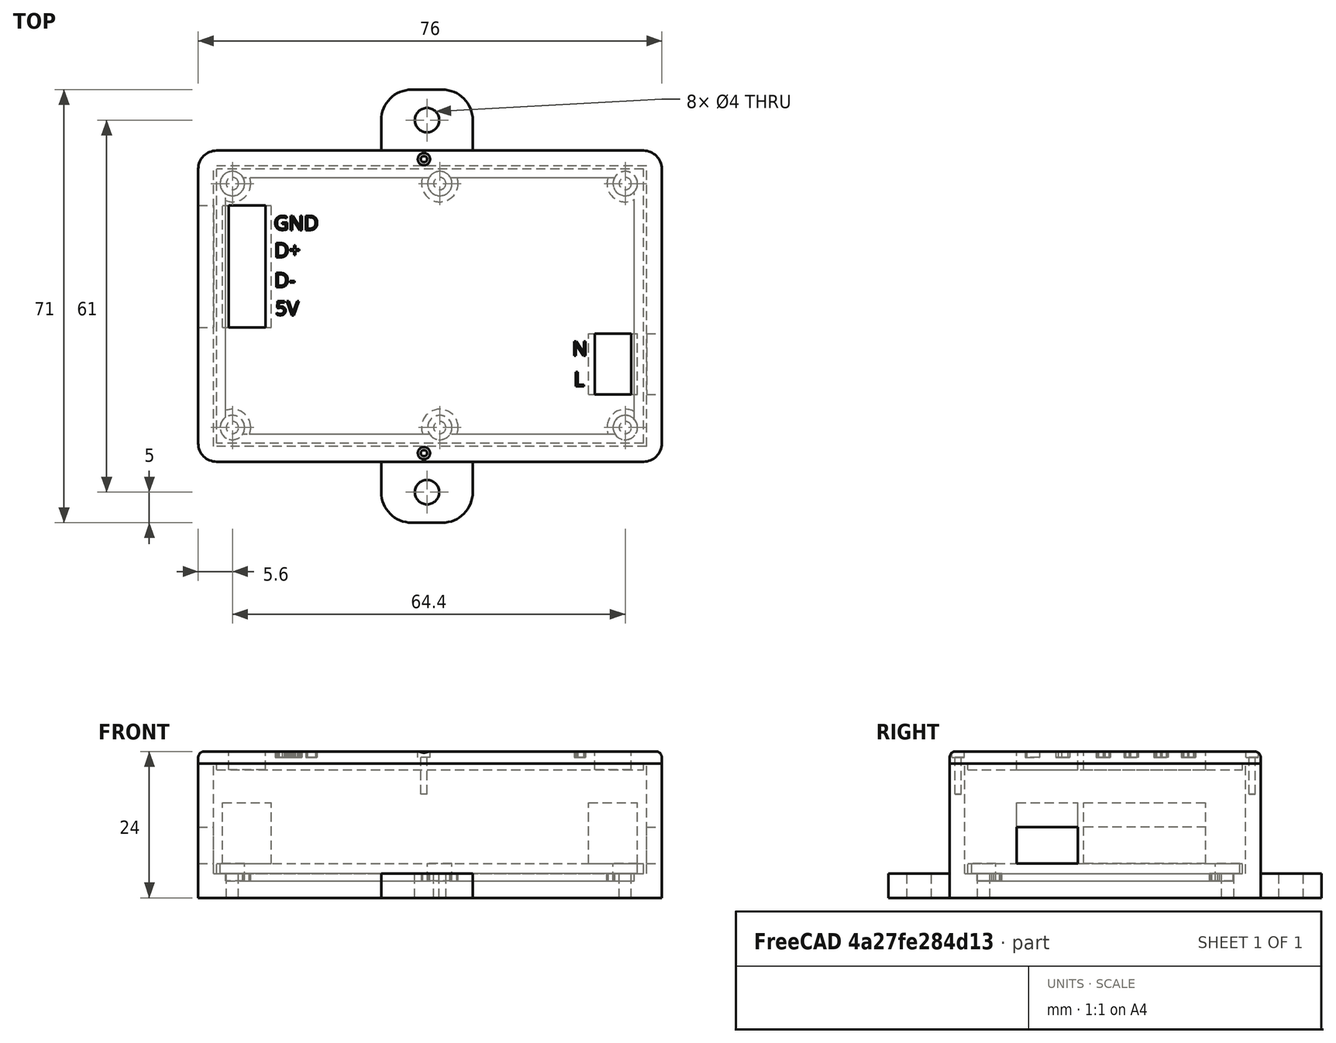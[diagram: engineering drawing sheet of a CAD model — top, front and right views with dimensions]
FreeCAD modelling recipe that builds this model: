
FCSTD DOCUMENT  (FreeCAD 0.17R13522 (Git))
Label: Caja Bridge TCP-RTU V1-230V
License: All rights reserved
LicenseURL: http://en.wikipedia.org/wiki/All_rights_reserved
objects: Part::Cylinder×26, Part::Cut×18, Part::Box×15, Part::MultiFuse×15, Part::Part2DObjectPython×6, Part::Extrusion×6, Part::Fillet×4
note: 90 computed .brp shape members not serialized (recipe doc carries the construction recipe); baked Part::Feature solids carry a one-line shape summary decoded from their .brp

FEATURE [Part::Box] Box  label="Cubo"
  AttacherType = Attacher::AttachEngine3D
  Height = 1.6
  Length = 70
  Width = 45
FEATURE [Part::Cylinder] Cylinder  label="Cilindro"
  Angle = 360
  AttacherType = Attacher::AttachEngine3D
  Height = 10
  Placement = pos=(2.6,2.6,-5) rot=(0,0,1;0rad)
  Radius = 2
FEATURE [Part::Cylinder] Cylinder001  label="Cilindro001"
  Angle = 360
  AttacherType = Attacher::AttachEngine3D
  Height = 10
  Placement = pos=(36.6,2.6,-5) rot=(0,0,1;0rad)
  Radius = 2
FEATURE [Part::Cylinder] Cylinder002  label="Cilindro002"
  Angle = 360
  AttacherType = Attacher::AttachEngine3D
  Height = 10
  Placement = pos=(36.6,42.6,-5) rot=(0,0,1;0rad)
  Radius = 2
FEATURE [Part::Cylinder] Cylinder003  label="Cilindro003"
  Angle = 360
  AttacherType = Attacher::AttachEngine3D
  Height = 10
  Placement = pos=(2.6,42.6,-5) rot=(0,0,1;0rad)
  Radius = 2
FEATURE [Part::Box] Box001  label="Cubo001"
  AttacherType = Attacher::AttachEngine3D
  Height = 10
  Length = 8
  Placement = pos=(1,19,1.6) rot=(0,0,1;0rad)
  Width = 20
FEATURE [Part::Box] Box002  label="Cubo002"
  AttacherType = Attacher::AttachEngine3D
  Height = 20
  Length = 71
  Placement = pos=(-0.5,-0.5,0) rot=(0,0,1;0rad)
  Width = 46
FEATURE [Part::Box] Box003  label="Cubo003"
  AttacherType = Attacher::AttachEngine3D
  Height = 22
  Length = 76
  Placement = pos=(-3,-3,-4) rot=(0,0,1;0rad)
  Width = 51
FEATURE [Part::Box] Box004  label="Cubo004"
  AttacherType = Attacher::AttachEngine3D
  Height = 1.5
  Length = 67
  Placement = pos=(1.5,1.5,-1.2) rot=(0,0,1;0rad)
  Width = 42
FEATURE [Part::MultiFuse] Fusion
  Refine = true
  Shapes = -> [Box,Box004]
FEATURE [Part::MultiFuse] Fusion001
  Refine = true
  Shapes = -> [Fusion,Box001]
FEATURE [Part::MultiFuse] Fusion002
  Refine = true
  Shapes = -> [Cylinder,Cylinder003,Cylinder002,Cylinder001]
FEATURE [Part::Cut] Cut  label="Electronica"
  Base = -> Fusion001
  Refine = true
  Tool = -> Fusion002
FEATURE [Part::Box] Box005  label="Cubo005"
  AttacherType = Attacher::AttachEngine3D
  Height = 1.5
  Length = 67
  Placement = pos=(1.5,1.5,-1.2) rot=(0,0,1;0rad)
  Width = 42
FEATURE [Part::MultiFuse] Fusion003
  Refine = true
  Shapes = -> [Box002,Box005]
FEATURE [Part::Box] Box006  label="Cubo006"
  AttacherType = Attacher::AttachEngine3D
  Height = 6
  Length = 22
  Placement = pos=(-10,19,1.6) rot=(0,0,1;0rad)
  Width = 20
FEATURE [Part::Box] Box007  label="Cubo007"
  AttacherType = Attacher::AttachEngine3D
  Height = 2
  Length = 76
  Placement = pos=(-3,-3,18) rot=(0,0,1;0rad)
  Width = 51
FEATURE [Part::Box] Box008  label="Cubo008"
  AttacherType = Attacher::AttachEngine3D
  Height = 3
  Length = 70
  Placement = pos=(0,0,17) rot=(0,0,1;0rad)
  Width = 45
FEATURE [Part::Cylinder] Cylinder004  label="Cilindro004"
  Angle = 360
  AttacherType = Attacher::AttachEngine3D
  Height = 10
  Placement = pos=(2.6,2.6,-5) rot=(0,0,1;0rad)
  Radius = 1
FEATURE [Part::Cylinder] Cylinder005  label="Cilindro005"
  Angle = 360
  AttacherType = Attacher::AttachEngine3D
  Height = 10
  Placement = pos=(36.6,2.6,-5) rot=(0,0,1;0rad)
  Radius = 1
FEATURE [Part::Cylinder] Cylinder006  label="Cilindro006"
  Angle = 360
  AttacherType = Attacher::AttachEngine3D
  Height = 10
  Placement = pos=(36.6,42.6,-5) rot=(0,0,1;0rad)
  Radius = 1
FEATURE [Part::Cylinder] Cylinder007  label="Cilindro007"
  Angle = 360
  AttacherType = Attacher::AttachEngine3D
  Height = 10
  Placement = pos=(2.6,42.6,-5) rot=(0,0,1;0rad)
  Radius = 1
FEATURE [Part::Cylinder] Cylinder008  label="Cilindro008"
  Angle = 360
  AttacherType = Attacher::AttachEngine3D
  Height = 3
  Placement = pos=(2.6,42.6,-3) rot=(0,0,1;0rad)
  Radius = 3
FEATURE [Part::Cylinder] Cylinder009  label="Cilindro009"
  Angle = 360
  AttacherType = Attacher::AttachEngine3D
  Height = 3
  Placement = pos=(36.6,2.6,-3) rot=(0,0,1;0rad)
  Radius = 3
FEATURE [Part::Cylinder] Cylinder010  label="Cilindro010"
  Angle = 360
  AttacherType = Attacher::AttachEngine3D
  Height = 3
  Placement = pos=(2.6,2.6,-3) rot=(0,0,1;0rad)
  Radius = 3
FEATURE [Part::Cylinder] Cylinder011  label="Cilindro011"
  Angle = 360
  AttacherType = Attacher::AttachEngine3D
  Height = 3
  Placement = pos=(36.6,42.6,-3) rot=(0,0,1;0rad)
  Radius = 3
FEATURE [Part::Cut] Cut001
  Base = -> Box003
  Refine = true
  Tool = -> Fusion003
FEATURE [Part::Cut] Cut002
  Base = -> Cut001
  Refine = true
  Tool = -> Box006
FEATURE [Part::MultiFuse] Fusion005
  Refine = true
  Shapes = -> [Cylinder008,Cut002,Cylinder011,Cylinder010,Cylinder009]
FEATURE [Part::MultiFuse] Fusion006
  Refine = true
  Shapes = -> [Cylinder007,Cylinder005,Cylinder004,Cylinder006]
FEATURE [Part::Cut] Cut003  label="Caja"
  Base = -> Fusion005
  Refine = true
  Tool = -> Fusion006
FEATURE [Part::MultiFuse] Fusion007
  Refine = true
  Shapes = -> [Box007,Box008]
FEATURE [Part::Cylinder] Cylinder012  label="Cilindro012"
  Angle = 360
  AttacherType = Attacher::AttachEngine3D
  Height = 10
  Placement = pos=(19,-1.6,13) rot=(0,0,1;0rad)
  Radius = 0.5
FEATURE [Part::Cylinder] Cylinder013  label="Cilindro013"
  Angle = 360
  AttacherType = Attacher::AttachEngine3D
  Height = 10
  Placement = pos=(19,46.6,13) rot=(0,0,1;0rad)
  Radius = 0.5
FEATURE [Part::MultiFuse] Fusion008
  Placement = pos=(15,0,0) rot=(0,0,1;0rad)
  Refine = true
  Shapes = -> [Cylinder012,Cylinder013]
FEATURE [Part::Cylinder] Cylinder014  label="Cilindro014"
  Angle = 360
  AttacherType = Attacher::AttachEngine3D
  Height = 10
  Placement = pos=(19,46.6,13) rot=(0,0,1;0rad)
  Radius = 0.5
FEATURE [Part::Cylinder] Cylinder015  label="Cilindro015"
  Angle = 360
  AttacherType = Attacher::AttachEngine3D
  Height = 10
  Placement = pos=(19,-1.6,13) rot=(0,0,1;0rad)
  Radius = 0.5
FEATURE [Part::MultiFuse] Fusion009
  Placement = pos=(15,0,0) rot=(0,0,1;0rad)
  Refine = true
  Shapes = -> [Cylinder015,Cylinder014]
FEATURE [Part::Cylinder] Cylinder016  label="Cilindro016"
  Angle = 360
  AttacherType = Attacher::AttachEngine3D
  Height = 10
  Placement = pos=(19,-1.6,19) rot=(0,0,1;0rad)
  Radius = 1
FEATURE [Part::Cylinder] Cylinder017  label="Cilindro017"
  Angle = 360
  AttacherType = Attacher::AttachEngine3D
  Height = 10
  Placement = pos=(19,46.6,19) rot=(0,0,1;0rad)
  Radius = 1
FEATURE [Part::MultiFuse] Fusion010
  Placement = pos=(15,0,0) rot=(0,0,1;0rad)
  Refine = true
  Shapes = -> [Cylinder016,Cylinder017]
FEATURE [Part::Box] Box009  label="Cubo009"
  AttacherType = Attacher::AttachEngine3D
  Height = 4
  Length = 15
  Placement = pos=(12,-13,-4) rot=(0,0,1;0rad)
  Width = 10
FEATURE [Part::Cylinder] Cylinder018  label="Cilindro018"
  Angle = 360
  AttacherType = Attacher::AttachEngine3D
  Height = 10
  Placement = pos=(19.5,-8,-7) rot=(0,0,1;0rad)
  Radius = 2
FEATURE [Part::Cut] Cut007
  Base = -> Box009
  Placement = pos=(15,0,0) rot=(0,0,1;0rad)
  Refine = true
  Tool = -> Cylinder018
FEATURE [Part::Cylinder] Cylinder019  label="Cilindro019"
  Angle = 360
  AttacherType = Attacher::AttachEngine3D
  Height = 10
  Placement = pos=(19.5,-8,-7) rot=(0,0,1;0rad)
  Radius = 2
FEATURE [Part::Box] Box010  label="Cubo010"
  AttacherType = Attacher::AttachEngine3D
  Height = 4
  Length = 15
  Placement = pos=(12,-13,-4) rot=(0,0,1;0rad)
  Width = 10
FEATURE [Part::Cut] Cut008
  Base = -> Box010
  Placement = pos=(15,61,0) rot=(0,0,1;0rad)
  Refine = true
  Tool = -> Cylinder019
FEATURE [Part::Fillet] Fillet
  Base = -> Fusion007
  Edges = 4 edges r=3: [Edge1,Edge3,Edge6,Edge9]
FEATURE [Part::Fillet] Fillet003
  Base = -> Fillet
  Edges = 4 edges r=1: [Edge1,Edge7,Edge8,Edge11]
FEATURE [Part::Cut] Cut009
  Base = -> Fillet003
  Refine = true
  Tool = -> Fusion010
FEATURE [Part::Cut] Cut010  label="Tapa V2"
  Base = -> Cut009
  Refine = true
  Tool = -> Fusion009
FEATURE [Part::Box] Box011  label="Cubo011"
  AttacherType = Attacher::AttachEngine3D
  Height = 48
  Length = 6
  Placement = pos=(2,19,1.6) rot=(0,0,1;0rad)
  Width = 20
FEATURE [Part::Cut] Cut011
  Base = -> Cut010
  Refine = true
  Tool = -> Box011
FEATURE [Part::Part2DObjectPython] ShapeString  label="GND"  # Draft 2D object (typed FeaturePython)
  FontFile = <path>
  Placement = pos=(9.41125,34.9742,20) rot=(0,0,1;0rad)
  Size = 3
  String = GND
  Tracking = 0
FEATURE [Part::Part2DObjectPython] ShapeString001  # Draft 2D object (typed FeaturePython)
  FontFile = C:/Program Files/FreeCAD 0.17/OpenSans-Regular.ttf
  Placement = pos=(9.47171,30.4997,20) rot=(0,0,1;0rad)
  Size = 3
  String = D+
  Tracking = 0
FEATURE [Part::Part2DObjectPython] ShapeString002  # Draft 2D object (typed FeaturePython)
  FontFile = C:/Program Files/FreeCAD 0.17/OpenSans-Regular.ttf
  Placement = pos=(9.47171,25.6019,20) rot=(0,0,1;0rad)
  Size = 3
  String = D-
  Tracking = 0
FEATURE [Part::Part2DObjectPython] ShapeString003  # Draft 2D object (typed FeaturePython)
  FontFile = C:/Program Files/FreeCAD 0.17/OpenSans-Regular.ttf
  Placement = pos=(9.65311,21.0064,20) rot=(0,0,1;0rad)
  Size = 3
  String = 5V
  Tracking = 0
FEATURE [Part::Extrusion] Extrude
  Base = -> ShapeString
  Dir = (0,0,-1)
  DirMode = 0
  FaceMakerClass = Part::FaceMakerBullseye
  LengthFwd = 1
  LengthRev = 0
  Solid = true
  Symmetric = false
FEATURE [Part::Extrusion] Extrude001
  Base = -> ShapeString001
  Dir = (0,0,-1)
  DirMode = 0
  FaceMakerClass = Part::FaceMakerBullseye
  LengthFwd = 1
  LengthRev = 0
  Solid = true
  Symmetric = false
FEATURE [Part::Extrusion] Extrude002
  Base = -> ShapeString002
  Dir = (0,0,-1)
  DirMode = 0
  FaceMakerClass = Part::FaceMakerBullseye
  LengthFwd = 1
  LengthRev = 0
  Solid = true
  Symmetric = false
FEATURE [Part::Extrusion] Extrude003
  Base = -> ShapeString003
  Dir = (0,0,-1)
  DirMode = 0
  FaceMakerClass = Part::FaceMakerBullseye
  LengthFwd = 1
  LengthRev = 0
  Solid = true
  Symmetric = false
FEATURE [Part::MultiFuse] Fusion012
  Refine = true
  Shapes = -> [Extrude003,Extrude,Extrude001,Extrude002]
FEATURE [Part::Cylinder] Cylinder020  label="Cilindro020"
  Angle = 360
  AttacherType = Attacher::AttachEngine3D
  Height = 10
  Placement = pos=(67,42.6,-5) rot=(0,0,1;0rad)
  Radius = 2
FEATURE [Part::Cylinder] Cylinder021  label="Cilindro021"
  Angle = 360
  AttacherType = Attacher::AttachEngine3D
  Height = 10
  Placement = pos=(67,2.6,-5) rot=(0,0,1;0rad)
  Radius = 2
FEATURE [Part::Cut] Cut013
  Base = -> Cut
  Refine = true
  Tool = -> Cylinder020
FEATURE [Part::Cut] Cut014  label="Electronica001"
  Base = -> Cut013
  Refine = true
  Tool = -> Cylinder021
FEATURE [Part::Box] Box012  label="Cubo012"
  AttacherType = Attacher::AttachEngine3D
  Height = 10
  Length = 8
  Placement = pos=(61,8,1.6) rot=(0,0,1;0rad)
  Width = 10
FEATURE [Part::MultiFuse] Fusion013  label="Electronica 230v"
  Refine = true
  Shapes = -> [Cut014,Box012]
FEATURE [Part::Cut] Cut006
  Base = -> Cut003
  Refine = true
  Tool = -> Fusion008
FEATURE [Part::MultiFuse] Fusion011
  Refine = true
  Shapes = -> [Cut006,Cut008,Cut007]
FEATURE [Part::Fillet] Fillet001
  Base = -> Fusion011
  Edges = 4 edges r=5: [Edge38,Edge44,Edge61,Edge66]
FEATURE [Part::Fillet] Fillet002  label="Caja V1"
  Base = -> Fillet001
  Edges = 4 edges r=3: [Edge16,Edge18,Edge41,Edge50]
FEATURE [Part::Cylinder] Cylinder022  label="Cilindro022"
  Angle = 360
  AttacherType = Attacher::AttachEngine3D
  Height = 3
  Placement = pos=(67,42.6,-3) rot=(0,0,1;0rad)
  Radius = 3
FEATURE [Part::Cylinder] Cylinder023  label="Cilindro023"
  Angle = 360
  AttacherType = Attacher::AttachEngine3D
  Height = 3
  Placement = pos=(67,2.6,-3) rot=(0,0,1;0rad)
  Radius = 3
FEATURE [Part::Cylinder] Cylinder024  label="Cilindro024"
  Angle = 360
  AttacherType = Attacher::AttachEngine3D
  Height = 10
  Placement = pos=(67,2.6,-5) rot=(0,0,1;0rad)
  Radius = 1
FEATURE [Part::Cylinder] Cylinder025  label="Cilindro025"
  Angle = 360
  AttacherType = Attacher::AttachEngine3D
  Height = 10
  Placement = pos=(67,42.6,-5) rot=(0,0,1;0rad)
  Radius = 1
FEATURE [Part::MultiFuse] Fusion014
  Refine = true
  Shapes = -> [Cylinder023,Cylinder022,Fillet002]
FEATURE [Part::Cut] Cut015
  Base = -> Fusion014
  Refine = true
  Tool = -> Cylinder025
FEATURE [Part::Cut] Cut016
  Base = -> Cut015
  Refine = true
  Tool = -> Cylinder024
FEATURE [Part::Box] Box013  label="Cubo013"
  AttacherType = Attacher::AttachEngine3D
  Height = 6
  Length = 22
  Placement = pos=(60,8,1.6) rot=(0,0,1;0rad)
  Width = 10
FEATURE [Part::Cut] Cut017  label="Caja V1-230"
  Base = -> Cut016
  Refine = true
  Tool = -> Box013
FEATURE [Part::Cut] Cut018
  Base = -> Cut011
  Refine = true
  Tool = -> Fusion012
FEATURE [Part::Box] Box014  label="Cubo014"
  AttacherType = Attacher::AttachEngine3D
  Height = 48
  Length = 6
  Placement = pos=(62,8,1.6) rot=(0,0,1;0rad)
  Width = 10
FEATURE [Part::Cut] Cut019
  Base = -> Cut018
  Refine = true
  Tool = -> Box014
FEATURE [Part::Part2DObjectPython] ShapeString004  # Draft 2D object (typed FeaturePython)
  FontFile = C:/Program Files/FreeCAD 0.17/OpenSans-Regular.ttf
  Placement = pos=(58.3377,14.3872,20) rot=(0,0,1;0rad)
  Size = 3
  String = N
  Tracking = 0
FEATURE [Part::Part2DObjectPython] ShapeString005  # Draft 2D object (typed FeaturePython)
  FontFile = C:/Program Files/FreeCAD 0.17/OpenSans-Regular.ttf
  Placement = pos=(58.5796,9.36849,20) rot=(0,0,1;0rad)
  Size = 3
  String = L
  Tracking = 0
FEATURE [Part::Extrusion] Extrude004
  Base = -> ShapeString004
  Dir = (0,0,-1)
  DirMode = 0
  FaceMakerClass = Part::FaceMakerBullseye
  LengthFwd = 1
  LengthRev = 0
  Solid = true
  Symmetric = false
FEATURE [Part::Extrusion] Extrude005
  Base = -> ShapeString005
  Dir = (0,0,-1)
  DirMode = 0
  FaceMakerClass = Part::FaceMakerBullseye
  LengthFwd = 1
  LengthRev = 0
  Solid = true
  Symmetric = false
FEATURE [Part::MultiFuse] Fusion015
  Refine = true
  Shapes = -> [Extrude005,Extrude004]
FEATURE [Part::Cut] Cut020  label="Tapa V1-230"
  Base = -> Cut019
  Refine = true
  Tool = -> Fusion015
note: 1 file-system path scrubbed to <path> (originals preserved in the JSON sidecar)
